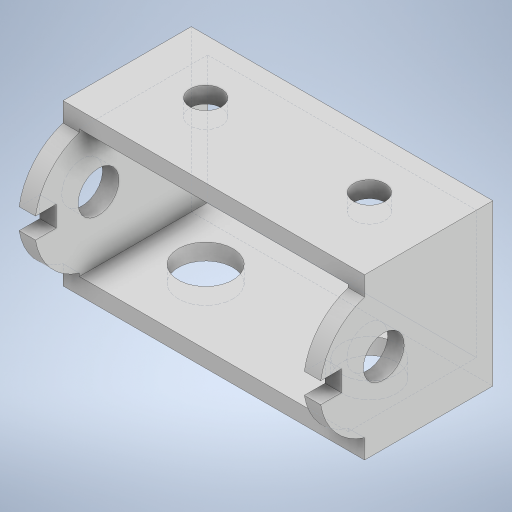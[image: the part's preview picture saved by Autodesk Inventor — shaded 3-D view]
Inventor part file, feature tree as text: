
AUTODESK INVENTOR PART (.ipt)
format: ipt  version: 2023 (Build 270158000, 158)  size: 299,008 bytes
history: native  units: mm
features: extrude x5, sketch x5, pattern_linear x1, mirror x1
ambient origin geometry x8: Origin, YZ Plane, XZ Plane, XY Plane, X Axis, Y Axis, Z Axis, Center Point
bodies: Solid1 (feature_tree)
feature tree (12):
  extrude  "Extrusion1"  Depth=3.8mm
  pattern_linear  "Rectangular Pattern1"  Count1=2 Spacing1=52.25mm
  extrude  "Extrusion3"  Depth=10.0mm
  extrude  "Extrusion4"  Depth=3.0mm TaperAngle=0.0deg
  mirror  "Mirror1"
  extrude  "Extrusion9"  TaperAngle=0.0deg  [1 undecoded]
  extrude  "Extrusion10"  Depth=10.0mm
  sketch  "Sketch1"  dims[d0=23.4mm d1=3.8mm]
  sketch  "Sketch3"  dims[d2=7.75mm]
  sketch  "Sketch4"  dims[d3=7.5mm]
  sketch  "Sketch9"  dims[d4=3.0mm d5=0.0mm d6=20.0mm d8=52.25mm]
  sketch  "Sketch10"  dims[d9=20.0mm d12=3.5mm d13=3.0mm d14=0.0mm d15=0.0mm d16=0.0mm d30=5.7625mm d31=30.0mm d32=10.0mm d33=10.0mm d34=0.0mm d35=10.0mm d36=10.0mm d37=0.0mm]
note: 1 required parameter value undecoded (feature->parameter linkage not recoverable at this tier; creation-order binding heuristic only, values carry confidence <= 0.55)
